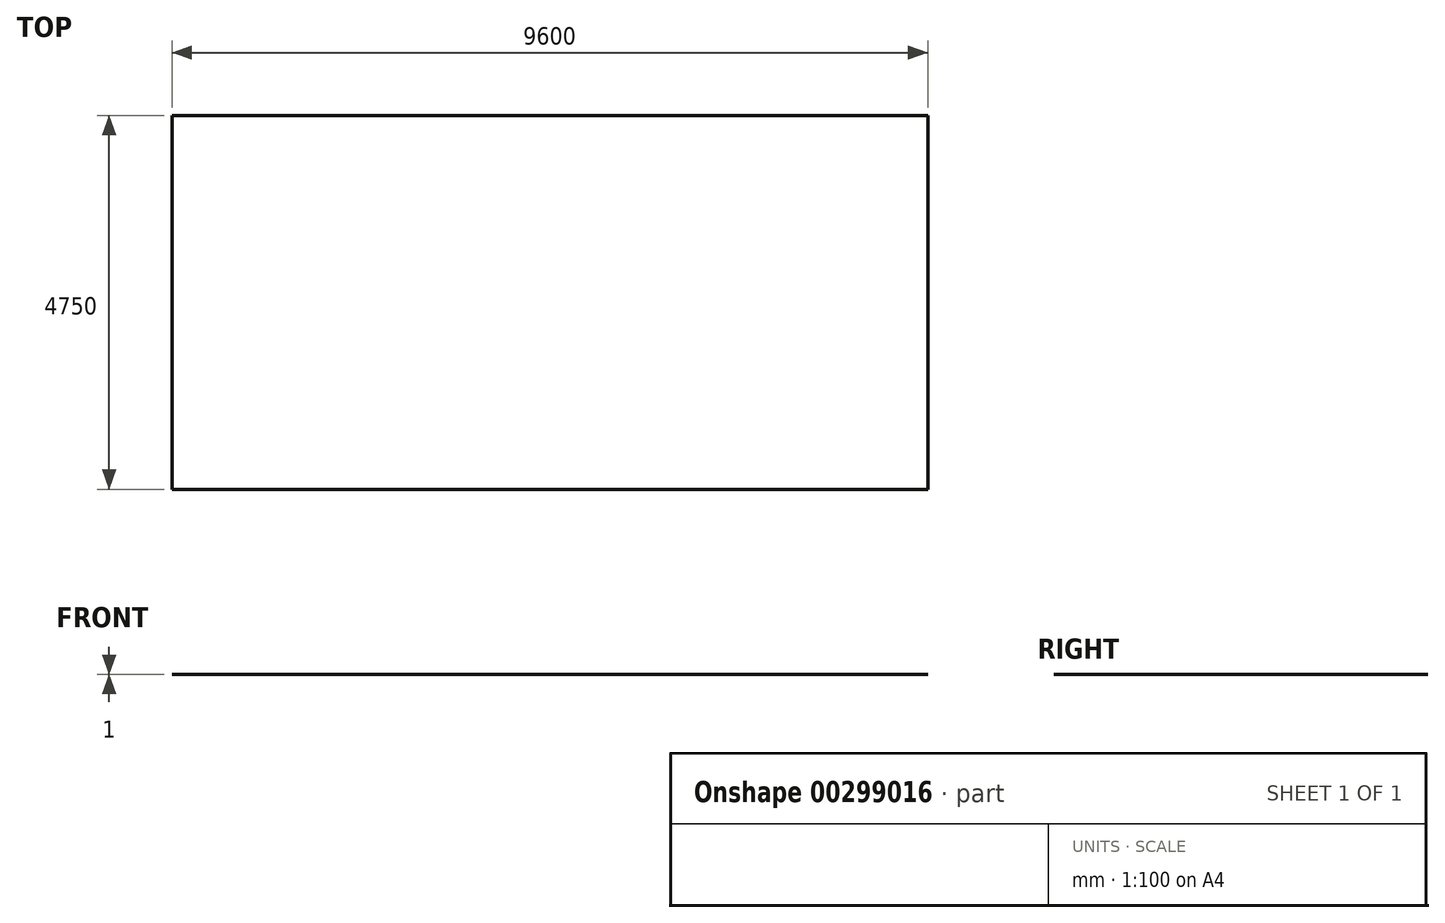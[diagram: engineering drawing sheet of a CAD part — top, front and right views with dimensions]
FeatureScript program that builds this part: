
annotation { "Feature Type Name" : "Feature", "Feature Type Description" : "" }
export const myFeature = defineFeature(function(context is Context, id is Id, definition is map)
    precondition{}
    {
        {
            var Q0;
            Q0=qCreatedBy(makeId("Top.planeOp"),FACE);
            var sketch = newSketch(context, id + "F0", { "sketchPlane" : qUnion([Q0])});
            skLineSegment(sketch, "E0.bottom", {"start": v(4800, -2375) * mm, "end": v(-4800, -2375) * mm});
            skLineSegment(sketch, "E0.top", {"start": v(4800, 2375) * mm, "end": v(-4800, 2375) * mm});
            skLineSegment(sketch, "E0.left", {"start": v(4800, -2375) * mm, "end": v(4800, 2375) * mm});
            skLineSegment(sketch, "E0.right", {"start": v(-4800, -2375) * mm, "end": v(-4800, 2375) * mm});
            skPoint(sketch, "E0.middle", {"position": v(0, 0) * mm});
            skSolve(sketch);
        }
        {
            var Q0;
            Q0=makeQuery(id+"F0.imprint","IMPRINT",FACE,{"disambiguationData":[TD([[makeQuery(id+"F0.imprint","IMPRINT",EDGE,{"derivedFrom":sQuery(id+"F0.wireOp",EDGE,"E0.bottom")}),-1.0]])]});
            extrude(context, id + "F1", {"entities" : qUnion([Q0]), "depth" : 1 * mm});
        }
    });
